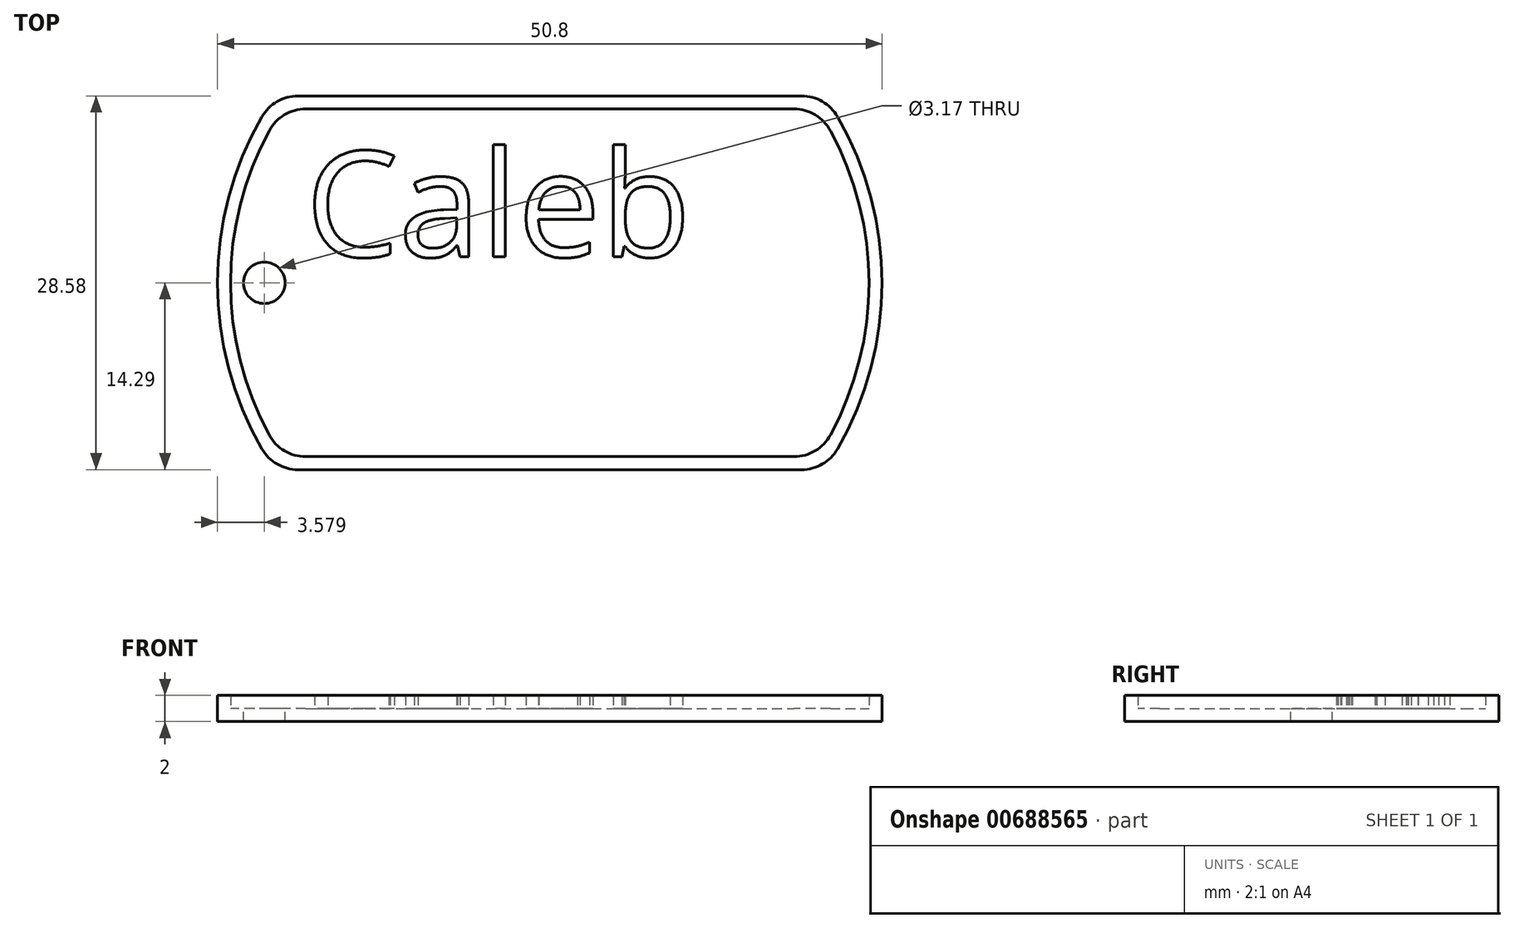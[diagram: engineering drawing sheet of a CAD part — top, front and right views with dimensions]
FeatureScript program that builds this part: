
annotation { "Feature Type Name" : "Feature", "Feature Type Description" : "" }
export const myFeature = defineFeature(function(context is Context, id is Id, definition is map)
    precondition{}
    {
        {
            var Q0;
            Q0=qCreatedBy(makeId("Top.planeOp"),FACE);
            var sketch = newSketch(context, id + "F0", { "sketchPlane" : qUnion([Q0])});
            skArc(sketch, "E0", {"start": v(-22, 12.7) * mm, "mid": v(-25.4, 0) * mm, "end": v(-22, -12.7) * mm});
            skLineSegment(sketch, "E1.top", {"start": v(-19.25, -14.29) * mm, "end": v(19.25, -14.29) * mm});
            skArc(sketch, "E2.trimOffspring", {"start": v(22, -12.7) * mm, "mid": v(25.4, 0) * mm, "end": v(22, 12.7) * mm});
            skLineSegment(sketch, "E3", {"start": v(-19.25, 14.29) * mm, "end": v(19.25, 14.29) * mm});
            skPoint(sketch, "E4.visualSharp", {"position": v(-21, 14.29) * mm});
            skArc(sketch, "E4.filletArc", {"start": v(-19.25, 14.29) * mm, "mid": v(-20.83, 13.86) * mm, "end": v(-22, 12.7) * mm});
            skPoint(sketch, "E5.visualSharp", {"position": v(21, 14.29) * mm});
            skArc(sketch, "E5.filletArc", {"start": v(22, 12.7) * mm, "mid": v(20.83, 13.86) * mm, "end": v(19.25, 14.29) * mm});
            skPoint(sketch, "E6.visualSharp", {"position": v(21, -14.29) * mm});
            skArc(sketch, "E6.filletArc", {"start": v(19.25, -14.29) * mm, "mid": v(20.83, -13.86) * mm, "end": v(22, -12.7) * mm});
            skPoint(sketch, "E7.visualSharp", {"position": v(-21, -14.29) * mm});
            skArc(sketch, "E7.filletArc", {"start": v(-22, -12.7) * mm, "mid": v(-20.83, -13.86) * mm, "end": v(-19.25, -14.29) * mm});
            skSolve(sketch);
        }
        {
            var Q0;
            Q0=makeQuery(id+"F0.imprint","IMPRINT",FACE,{"disambiguationData":[TD([[makeQuery(id+"F0.imprint","IMPRINT",EDGE,{"derivedFrom":sQuery(id+"F0.wireOp",EDGE,"E0")}),1.0]])]});
            extrude(context, id + "F1", {"entities" : qUnion([Q0]), "depth" : 1 * mm, "offsetDistance" : 25.4 * mm});
        }
        {
            var Q0;
            Q0=makeQuery(id+"F1.opExtrude","CAP_FACE",FACE,{"disambiguationData":[OSD([sQuery(id+"F0.wireOp",EDGE,"E0"),sQuery(id+"F0.wireOp",EDGE,"E1.top"),sQuery(id+"F0.wireOp",EDGE,"E2.trimOffspring"),sQuery(id+"F0.wireOp",EDGE,"E3"),sQuery(id+"F0.wireOp",EDGE,"E4.filletArc"),sQuery(id+"F0.wireOp",EDGE,"E5.filletArc"),sQuery(id+"F0.wireOp",EDGE,"E6.filletArc"),sQuery(id+"F0.wireOp",EDGE,"E7.filletArc")])],"isStart":false});
            var sketch = newSketch(context, id + "F2", { "sketchPlane" : qUnion([Q0])});
            skLineSegment(sketch, "E8.0", {"start": v(-18.66, 13.29) * mm, "end": v(18.66, 13.29) * mm});
            skArc(sketch, "E8.1", {"start": v(-21.45, 11.63) * mm, "mid": v(-24.4, 0) * mm, "end": v(-21.45, -11.63) * mm});
            skLineSegment(sketch, "E8.2", {"start": v(-18.66, -13.29) * mm, "end": v(18.66, -13.29) * mm});
            skArc(sketch, "E8.3", {"start": v(21.45, -11.63) * mm, "mid": v(24.4, 0) * mm, "end": v(21.45, 11.63) * mm});
            skPoint(sketch, "E9.visualSharp", {"position": v(-20.46, 13.29) * mm});
            skArc(sketch, "E9.filletArc", {"start": v(-18.66, 13.29) * mm, "mid": v(-20.29, 12.84) * mm, "end": v(-21.45, 11.63) * mm});
            skPoint(sketch, "E10.visualSharp", {"position": v(20.46, 13.29) * mm});
            skArc(sketch, "E10.filletArc", {"start": v(21.45, 11.63) * mm, "mid": v(20.29, 12.84) * mm, "end": v(18.66, 13.29) * mm});
            skPoint(sketch, "E11.visualSharp", {"position": v(20.46, -13.29) * mm});
            skArc(sketch, "E11.filletArc", {"start": v(18.66, -13.29) * mm, "mid": v(20.29, -12.84) * mm, "end": v(21.45, -11.63) * mm});
            skPoint(sketch, "E12.visualSharp", {"position": v(-20.46, -13.29) * mm});
            skArc(sketch, "E12.filletArc", {"start": v(-21.45, -11.63) * mm, "mid": v(-20.29, -12.84) * mm, "end": v(-18.66, -13.29) * mm});
            skLineSegment(sketch, "E13.0", {"start": v(-19.25, 14.29) * mm, "end": v(19.25, 14.29) * mm});
            skArc(sketch, "E13.1", {"start": v(-22, 12.7) * mm, "mid": v(-25.4, 0) * mm, "end": v(-22, -12.7) * mm});
            skLineSegment(sketch, "E13.2", {"start": v(-19.25, -14.29) * mm, "end": v(19.25, -14.29) * mm});
            skArc(sketch, "E13.3", {"start": v(22, -12.7) * mm, "mid": v(25.4, 0) * mm, "end": v(22, 12.7) * mm});
            skPoint(sketch, "E14.visualSharp", {"position": v(-21, -14.29) * mm});
            skArc(sketch, "E14.filletArc", {"start": v(-22, -12.7) * mm, "mid": v(-20.83, -13.86) * mm, "end": v(-19.25, -14.29) * mm});
            skPoint(sketch, "E15.visualSharp", {"position": v(21, -14.29) * mm});
            skArc(sketch, "E15.filletArc", {"start": v(19.25, -14.29) * mm, "mid": v(20.83, -13.86) * mm, "end": v(22, -12.7) * mm});
            skPoint(sketch, "E16.visualSharp", {"position": v(21, 14.29) * mm});
            skArc(sketch, "E16.filletArc", {"start": v(22, 12.7) * mm, "mid": v(20.83, 13.86) * mm, "end": v(19.25, 14.29) * mm});
            skPoint(sketch, "E17.visualSharp", {"position": v(-21, 14.29) * mm});
            skArc(sketch, "E17.filletArc", {"start": v(-19.25, 14.29) * mm, "mid": v(-20.83, 13.86) * mm, "end": v(-22, 12.7) * mm});
            skSolve(sketch);
        }
        {
            var Q0;
            Q0=makeQuery(id+"F2.imprint","IMPRINT",FACE,{"disambiguationData":[TD([[makeQuery(id+"F2.imprint","IMPRINT",EDGE,{"derivedFrom":sQuery(id+"F2.wireOp",EDGE,"E8.0")}),1.0]])]});
            extrude(context, id + "F3", {"entities" : qUnion([Q0]), "operationType" : NewBodyOperationType.ADD, "depth" : 1 * mm, "offsetDistance" : 25.4 * mm});
        }
        {
            var Q0;
            Q0=makeQuery(id+"F1.opExtrude","CAP_FACE",FACE,{"disambiguationData":[OSD([sQuery(id+"F0.wireOp",EDGE,"E0"),sQuery(id+"F0.wireOp",EDGE,"E1.top"),sQuery(id+"F0.wireOp",EDGE,"E2.trimOffspring"),sQuery(id+"F0.wireOp",EDGE,"E3"),sQuery(id+"F0.wireOp",EDGE,"E4.filletArc"),sQuery(id+"F0.wireOp",EDGE,"E5.filletArc"),sQuery(id+"F0.wireOp",EDGE,"E6.filletArc"),sQuery(id+"F0.wireOp",EDGE,"E7.filletArc")])],"isStart":false});
            var sketch = newSketch(context, id + "F4", { "sketchPlane" : qUnion([Q0])});
            skCircle(sketch, "E18", {"center": v(-21.82, 0) * mm, "radius": 1.59 * mm});
            skSolve(sketch);
        }
        {
            var Q0;
            Q0=makeQuery(id+"F4.imprint","IMPRINT",FACE,{"disambiguationData":[TD([[makeQuery(id+"F4.imprint","IMPRINT",EDGE,{"derivedFrom":sQuery(id+"F4.wireOp",EDGE,"E18")}),1.0]])]});
            extrude(context, id + "F5", {"entities" : qUnion([Q0]), "operationType" : NewBodyOperationType.REMOVE, "oppositeDirection" : true, "depth" : 1 * mm, "offsetDistance" : 25.4 * mm});
        }
        {
            var Q0;
            Q0=makeQuery(id+"F1.opExtrude","CAP_FACE",FACE,{"disambiguationData":[OSD([sQuery(id+"F0.wireOp",EDGE,"E0"),sQuery(id+"F0.wireOp",EDGE,"E1.top"),sQuery(id+"F0.wireOp",EDGE,"E2.trimOffspring"),sQuery(id+"F0.wireOp",EDGE,"E3"),sQuery(id+"F0.wireOp",EDGE,"E4.filletArc"),sQuery(id+"F0.wireOp",EDGE,"E5.filletArc"),sQuery(id+"F0.wireOp",EDGE,"E6.filletArc"),sQuery(id+"F0.wireOp",EDGE,"E7.filletArc")])],"isStart":false});
            var sketch = newSketch(context, id + "F6", { "sketchPlane" : qUnion([Q0])});
            skText(sketch, "E19", { "text": "Caleb", "fontName": "OpenSans-Regular.ttf"});
            const initialGuessF6  = {"E19": [-0.01866, 0.002, 1, 0, 0.00811]};
            skSetInitialGuess(sketch, initialGuessF6);
            skSolve(sketch);
        }
        {
            var Q0;
            Q0 = qSketchRegion(id + "F6", true);
            extrude(context, id + "F7", {"entities" : qUnion([Q0]), "operationType" : NewBodyOperationType.ADD, "depth" : 1 * mm, "offsetDistance" : 25.4 * mm});
        }
    });
